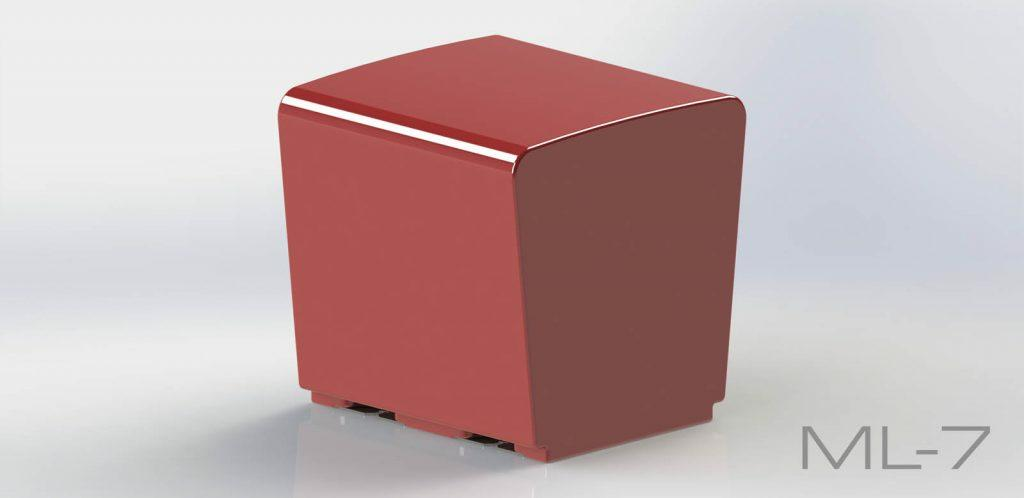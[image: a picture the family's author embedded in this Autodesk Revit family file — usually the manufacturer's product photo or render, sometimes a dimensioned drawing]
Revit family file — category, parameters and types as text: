
# Revit family: Modullaro ML 07
name_source: partatom
category: Furniture
revit_build: Autodesk Revit 2018 (Build: 20190510_1515(x64)
units: mm (PartAtom-declared; Revit-internal decimal feet)

## family parameters
Cut with Voids When Loaded = No
Host = Face
OmniClass Number = 23.40.10.11.14
OmniClass Title = Exterior Seating
Room Calculation Point = No
Shared = No

## types (1)
- Modullaro ML 07
    Default Elevation = 1219 mm
    Height = 500 mm  [stored 1.64042 ft]
    IfcExportAs = IfcFurnishingElement
    Length = 500 mm  [stored 1.64042 ft]
    Manufacturer = Astrini Design
    Material information = Colour choice from RAL colour standard. Customer may inquire about specific request regarding individual order.
    Model = Modullaro ML 07
    Operating temperature = -40°C to 80°C, ( -40°F to 176°F )
    Type Comments = Bench
    Type Image = ML-7.jpg
    URL = https://astrini-design.pl
    Weight (approximately) = 8.00 kg
    Width = 494 mm

note: [stored X ft] marks values corroborated as IEEE doubles in the binary element streams (Revit-internal decimal feet)
